# Revit family: Trapezblechhänger MU-S
name_source: partatom
category: Allgemeines Modell
revit_build: Autodesk Revit 2017 (Build: 20190507_1515(x64)
units: mm (PartAtom-declared; Revit-internal decimal feet)

## family parameters
Arbeitsebenenbasiert = Ja
Beim Laden mit Abzugskörper schneiden = Nein
Bemaßung runder Anschluss = Durchmesser verwenden
Gemeinsam genutzt = Ja
Immer vertikal = Nein
Kann Basisbauteil für Bewehrung sein = Nein
Raumberechnungspunkt = Nein
Teiletyp = Normal

## types (3) — shared parameters
Ausführung = eingeschweißte Mutter
Befestigungsloch = 9.5 mm
Breite Aufnahme (innen) = 22,5 mm
Breite Material = 25 mm
Fabrikat = MEFA
Firma = MEFA Befestigungs- und Montagesysteme GmbH
Höhe = 92.5 mm
Kurztext1 = Trapezblechhänger MU-S
Material = Stahl
Materialname = S235/DD11
Mengeneinheit = St
Oberflaeche = galvanisch verzinkt
Stärke Material = 3 mm  [stored 0.00984252 ft]
Vorgabe-Ansicht = 1219 mm
max. zul. Last = 2.00 kN
vpe = 100 St

## per-type parameters (varying)
| type | Anschlussgewinde | Artikelnummer | EAN | Gewicht | Gewicht pro Bauteil | Kurztext2 | Mutter DIN 928 | Trapezblechhänger |
| Trapezblechhänger MU-S M 8 | M8 | 0783900 | 4250928418845 | 0.11 kg | 0.11 kg | eingeschweißte Mutter M8 | Mutter DIN 928 : Mutter DIN 928 M 8 | Trapezblechhänger : MEFA Trapezblechhänger Bohrung 12 mm |
| Trapezblechhänger MU-S M10 | M10 | 0783935 | 4250928418852 | 0.12 kg | 0.12 kg | eingeschweißte Mutter M10 | Mutter DIN 928 : Mutter DIN 928 M10 | Trapezblechhänger : MEFA Trapezblechhänger Bohrung 12 mm |
| Trapezblechhänger MU-S M12 | M10 | 0783935 | 4250928418852 | 0.12 kg | 0.12 kg | eingeschweißte Mutter M10 | Mutter DIN 928 : Mutter DIN 928 M12 | Trapezblechhänger : MEFA Trapezblechhänger Bohrung 14 mm |

note: [stored X ft] marks values corroborated as IEEE doubles in the binary element streams (Revit-internal decimal feet)
